# Revit family: Roseta de superficie MM
name_source: partatom
category: Aparatos eléctricos
revit_build: Autodesk Revit 2016 (Build: 20150220_1215(x64)
units: mm (PartAtom-declared; Revit-internal decimal feet)

## family parameters
Anfitrión = Cara
Compartido = No
Corte con vacíos al cargar = No
Cota de conector redondo = Diámetro de uso
Mantener orientación de anotación = No
Número OmniClass = 23.80.50.11.11
Punto de cálculo de habitación = No
Tipo de pieza = Normal
Título OmniClass = Receptacle Terminal Units

## types (2) — shared parameters
CE45 (AltoxLargoxAncho) = 10 x 80 x 80 mm
Capacidad = 1 módulo 45
Compatibilidad = Gama 45
Composición = Cubeta, Marco, Bastidor, Tornillería marco (2ud), Tonillería montaje superficie (2ud)
Cv80 (AltoxLargoxAncho) = 45 x 80 x 80 mm
Código de montaje = D5020100
Descripción = Roseta de superficie MM
Elevación por defecto = 1200 mm
Fabricante = MMCONECTA
Instalación = Superficie
Materia prima = Policarbonato libre de halógenos
Modelo = Roseta de superficie CE45
Normativas = UNE 20451:1997 / Marcado CE
URL = http://www.mmconecta.com

## per-type parameters (varying)
| type | Acabado |
| Módulo /4 - Blanco | Blanco nieve RAL9019 |
| Módulo /6 - Grafito | Grafito RAL7021 |

## geometry (parser evidence)
native form markers: Blend x4
no freeform markers — native parametric forms only
